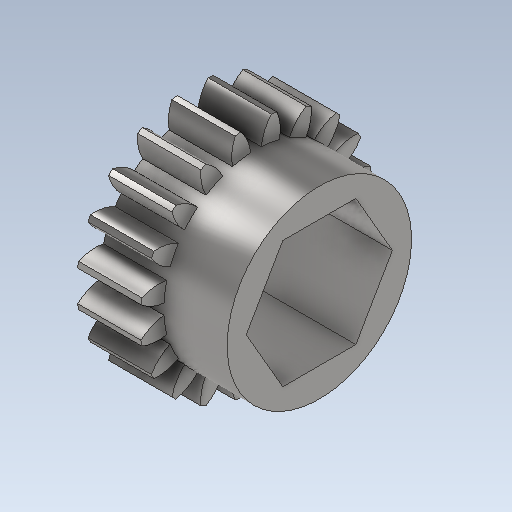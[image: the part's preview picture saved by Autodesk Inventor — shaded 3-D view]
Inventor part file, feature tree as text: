
AUTODESK INVENTOR PART (.ipt)
format: ipt  version: 2023 (Build 270158000, 158)  size: 688,128 bytes
history: native  units: in
note: dims shown in document units (in); Inventor stores cm internally (conversion verified against a paired STEP export)
features: sketch x3, other x1, revolve x1, extrude x1, hole x1, projected_geometry x1
ambient origin geometry x8: Origin, YZ Plane, XZ Plane, XY Plane, X Axis, Y Axis, Z Axis, Center Point
bodies: Solid1 (feature_tree)
feature tree (8):
  other  "TeethCuts"
  revolve  "Revolution1"  [1 undecoded]
  extrude  "Extrusion3"  Depth=0.1875in
  hole  "Hole1"  [1 undecoded]
  sketch  "Sketch3"  dims[d7=0.1875in d8=0.125in]
  sketch  "Sketch4"  dims[d9=0.1875in d10=0.1875in]
  projected_geometry  "Projected Loop1"
  sketch  "Sketch5"  dims[d12=2.4724in d13=0.13in d14=0.328in d15=0.375in d16=0.25in d17=0.5635in d18=1.0in d19=0.8108in d20=0.375in d21=0.0in d22=0.0in]
note: 2 required parameter values undecoded (feature->parameter linkage not recoverable at this tier; creation-order binding heuristic only, values carry confidence <= 0.55)